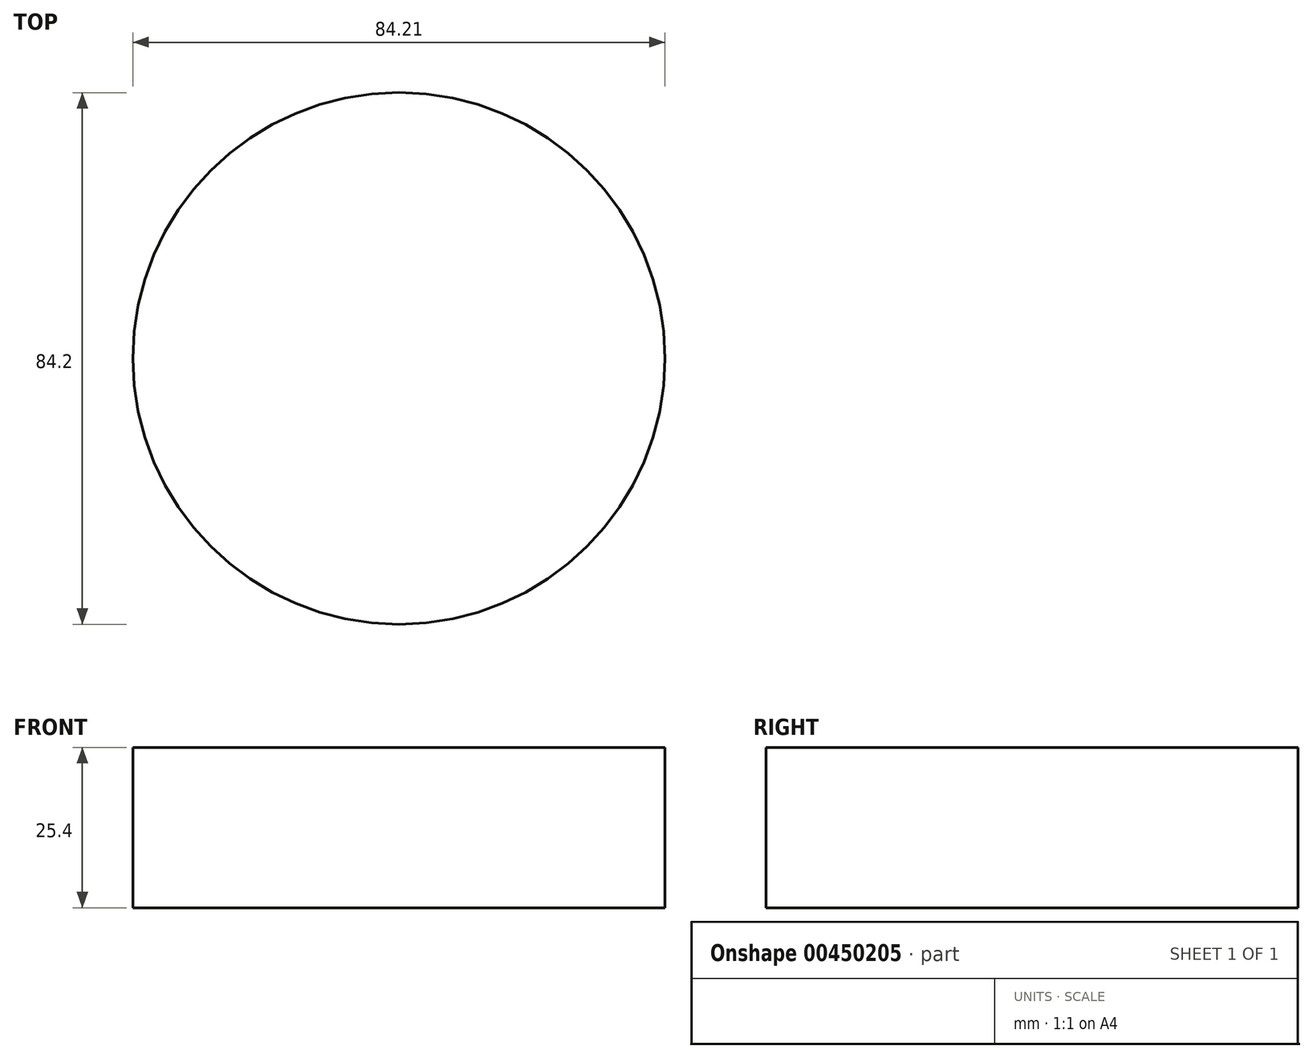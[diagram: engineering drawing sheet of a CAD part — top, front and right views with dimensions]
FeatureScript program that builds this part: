
annotation { "Feature Type Name" : "Feature", "Feature Type Description" : "" }
export const myFeature = defineFeature(function(context is Context, id is Id, definition is map)
    precondition{}
    {
        {
            var Q0;
            Q0=qCreatedBy(makeId("Top.planeOp"),FACE);
            var sketch = newSketch(context, id + "F0", { "sketchPlane" : qUnion([Q0])});
            skCircle(sketch, "E0", {"center": v(42.1, 0) * mm, "radius": 42.1 * mm});
            skSolve(sketch);
        }
        {
            var Q0;
            Q0 = qSketchRegion(id + "F0", true);
            extrude(context, id + "F1", {"entities" : qUnion([Q0]), "depth" : 25.4 * mm});
        }
    });
